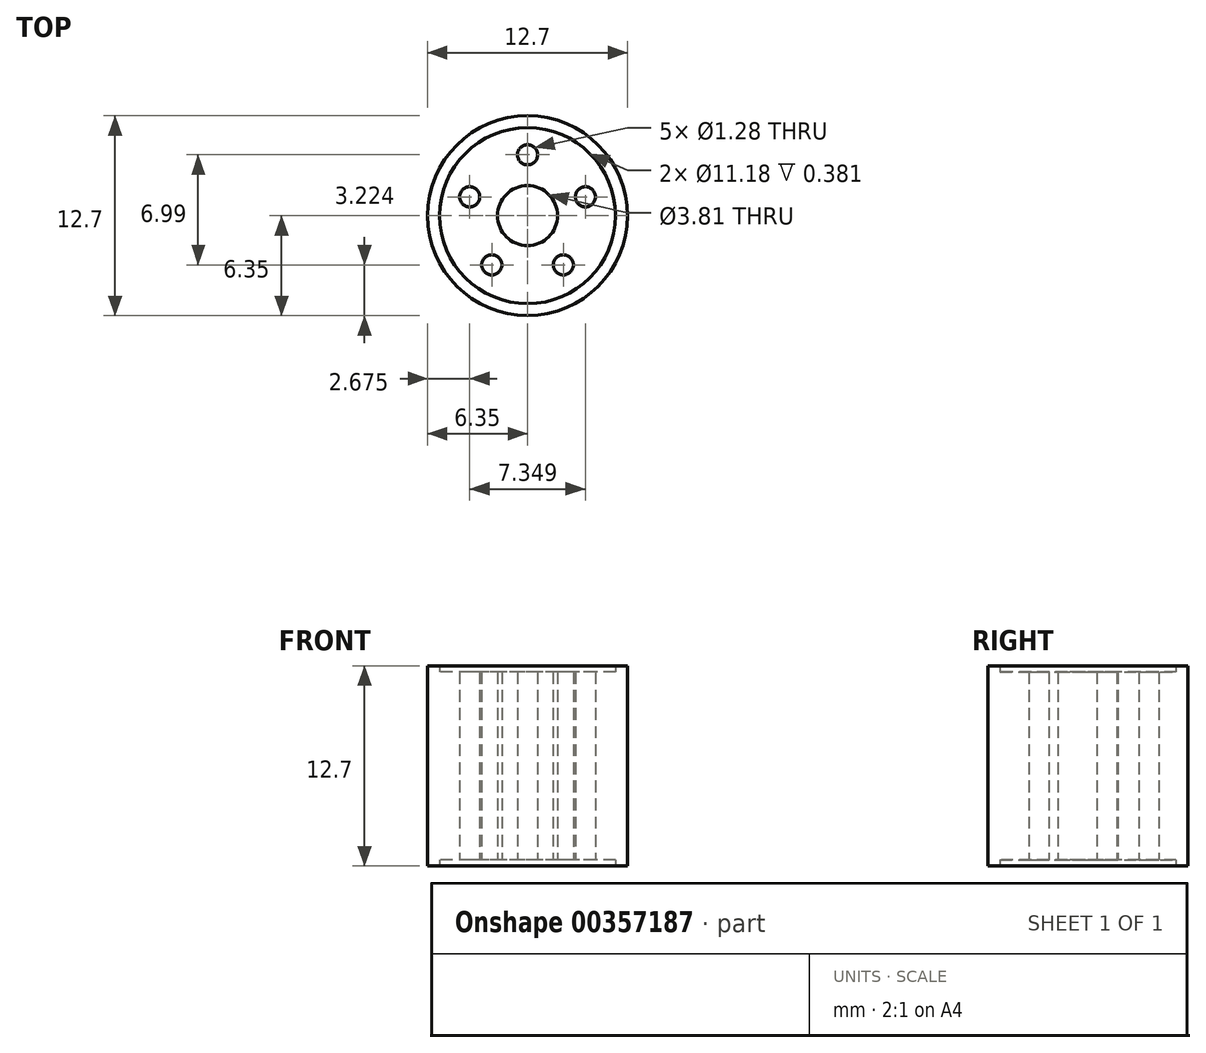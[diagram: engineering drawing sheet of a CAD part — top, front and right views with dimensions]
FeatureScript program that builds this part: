
annotation { "Feature Type Name" : "Feature", "Feature Type Description" : "" }
export const myFeature = defineFeature(function(context is Context, id is Id, definition is map)
    precondition{}
    {
        {
            var Q0;
            Q0=qCreatedBy(makeId("Top.planeOp"),FACE);
            var sketch = newSketch(context, id + "F0", { "sketchPlane" : qUnion([Q0])});
            skCircle(sketch, "E0", {"center": v(0, 0) * mm, "radius": 1.9 * mm});
            skCircle(sketch, "E1", {"center": v(0, 0) * mm, "radius": 5.59 * mm});
            skCircle(sketch, "E2", {"center": v(0, 0) * mm, "radius": 6.35 * mm});
            skCircle(sketch, "E3", {"center": v(0, 3.86) * mm, "radius": 0.64 * mm});
            skCircle(sketch, "E4.1.0", {"center": v(-3.67, 1.2) * mm, "radius": 0.64 * mm});
            skCircle(sketch, "E4.2.0", {"center": v(-2.27, -3.13) * mm, "radius": 0.64 * mm});
            skCircle(sketch, "E4.3.0", {"center": v(2.27, -3.13) * mm, "radius": 0.64 * mm});
            skCircle(sketch, "E4.4.0", {"center": v(3.67, 1.2) * mm, "radius": 0.64 * mm});
            skSolve(sketch);
        }
        {
            var Q0;
            Q0=makeQuery(id+"F0.imprint","IMPRINT",FACE,{"disambiguationData":[TD([[makeQuery(id+"F0.imprint","IMPRINT",EDGE,{"derivedFrom":sQuery(id+"F0.wireOp",EDGE,"E1")}),-1.0]])]});
            extrude(context, id + "F1", {"entities" : qUnion([Q0]), "endBound" : BoundingType.SYMMETRIC, "depth" : 12.7 * mm});
        }
        {
            var Q0;
            Q0=makeQuery(id+"F0.imprint","IMPRINT",FACE,{"disambiguationData":[TD([[makeQuery(id+"F0.imprint","IMPRINT",EDGE,{"derivedFrom":sQuery(id+"F0.wireOp",EDGE,"E0")}),-1.0]])]});
            extrude(context, id + "F2", {"entities" : qUnion([Q0]), "operationType" : NewBodyOperationType.ADD, "endBound" : BoundingType.SYMMETRIC, "depth" : 11.94 * mm});
        }
    });
